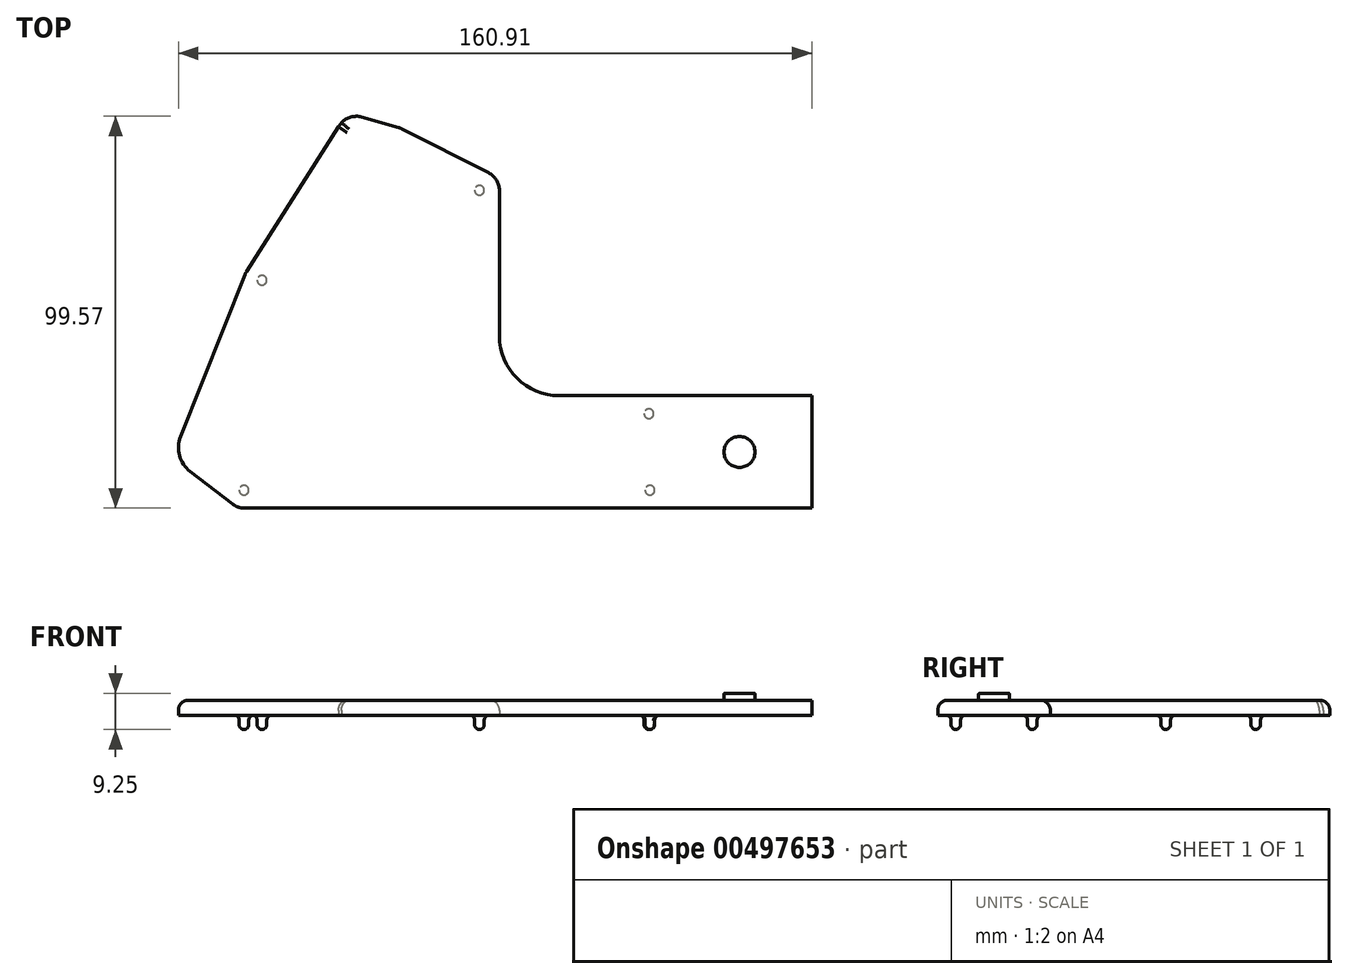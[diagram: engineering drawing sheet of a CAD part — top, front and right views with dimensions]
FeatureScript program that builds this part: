
annotation { "Feature Type Name" : "Feature", "Feature Type Description" : "" }
export const myFeature = defineFeature(function(context is Context, id is Id, definition is map)
    precondition{}
    {
        {
            var Q0;
            Q0=qCreatedBy(makeId("Top.planeOp"),FACE);
            var sketch = newSketch(context, id + "F0", { "sketchPlane" : qUnion([Q0])});
            skLineSegment(sketch, "E0.0", {"start": v(-43.43, -337.67) * mm, "end": v(-15.96, -337.67) * mm});
            skLineSegment(sketch, "E1.0", {"start": v(-160.03, -337.67) * mm, "end": v(-44.7, -337.67) * mm});
            skLineSegment(sketch, "E2.0", {"start": v(-43.43, -309.1) * mm, "end": v(-15.96, -309.1) * mm});
            skLineSegment(sketch, "E3.0", {"start": v(-80.1, -309.1) * mm, "end": v(-44.7, -309.1) * mm});
            skArc(sketch, "E4.0", {"start": v(-80.1, -309.1) * mm, "mid": v(-90.87, -304.63) * mm, "end": v(-95.34, -293.85) * mm});
            skLineSegment(sketch, "E5.0", {"start": v(-95.34, -293.85) * mm, "end": v(-95.34, -256.97) * mm});
            skArc(sketch, "E6.0", {"start": v(-95.34, -256.97) * mm, "mid": v(-96.09, -254.3) * mm, "end": v(-98.12, -252.43) * mm});
            skLineSegment(sketch, "E7.0", {"start": v(-98.12, -252.43) * mm, "end": v(-120.03, -241.33) * mm});
            skArc(sketch, "E8.0", {"start": v(-120.03, -241.33) * mm, "mid": v(-120.47, -241.13) * mm, "end": v(-120.93, -240.97) * mm});
            skLineSegment(sketch, "E9.0", {"start": v(-130.32, -238.3) * mm, "end": v(-120.93, -240.97) * mm});
            skArc(sketch, "E10.0", {"start": v(-130.32, -238.3) * mm, "mid": v(-133.1, -238.29) * mm, "end": v(-135.45, -239.74) * mm});
            skLineSegment(sketch, "E11.0", {"start": v(-136.2, -240.77) * mm, "end": v(-141.2, -248.63) * mm});
            skLineSegment(sketch, "E12.0", {"start": v(-151.3, -264.49) * mm, "end": v(-159.82, -277.9) * mm});
            skLineSegment(sketch, "E13.0", {"start": v(-159.82, -277.9) * mm, "end": v(-165.67, -292.62) * mm});
            skLineSegment(sketch, "E14.0", {"start": v(-172.6, -310.09) * mm, "end": v(-176.33, -319.47) * mm});
            skArc(sketch, "E15.0", {"start": v(-176.33, -319.47) * mm, "mid": v(-176.6, -324.3) * mm, "end": v(-173.9, -328.33) * mm});
            skPoint(sketch, "E16.0", {"position": v(-168.51, -332.47) * mm});
            skLineSegment(sketch, "E17.0", {"start": v(-173.9, -328.33) * mm, "end": v(-163.13, -336.61) * mm});
            skArc(sketch, "E18.0", {"start": v(-163.13, -336.61) * mm, "mid": v(-161.67, -337.4) * mm, "end": v(-160.03, -337.67) * mm});
            skLineSegment(sketch, "E19", {"start": v(-172.6, -310.09) * mm, "end": v(-165.67, -292.62) * mm});
            skLineSegment(sketch, "E20", {"start": v(-151.3, -264.49) * mm, "end": v(-141.2, -248.63) * mm});
            skLineSegment(sketch, "E21", {"start": v(-136.2, -240.77) * mm, "end": v(-135.45, -239.74) * mm});
            skLineSegment(sketch, "E22", {"start": v(-44.7, -309.1) * mm, "end": v(-43.43, -309.1) * mm});
            skLineSegment(sketch, "E23", {"start": v(-44.7, -337.67) * mm, "end": v(-43.43, -337.67) * mm});
            skLineSegment(sketch, "E24", {"start": v(-15.96, -337.67) * mm, "end": v(-15.96, -309.1) * mm});
            skSolve(sketch);
        }
        {
            var Q0;
            Q0=makeQuery(id+"F0.imprint","IMPRINT",FACE,{"disambiguationData":[TD([[makeQuery(id+"F0.imprint","IMPRINT",EDGE,{"derivedFrom":sQuery(id+"F0.wireOp",EDGE,"d1444f51-8acc-4532-b601-094db481933f.0")}),-1.0]])]});
            var Q1;
            Q1=makeQuery(id+"F0.imprint","IMPRINT",FACE,{"disambiguationData":[TD([[makeQuery(id+"F0.imprint","IMPRINT",EDGE,{"derivedFrom":sQuery(id+"F0.wireOp",EDGE,"E0.0")}),1.0]])]});
            var Q2;
            Q2 = qConstructionFilter(qBodyType(qCreatedBy(id + "F0" ,EDGE), BodyType.WIRE), ConstructionObject.NO);
            extrude(context, id + "F1", {"entities" : qUnion([Q0, Q1]), "surfaceEntities" : qUnion([Q2]), "depth" : 3.81 * mm, "offsetDistance" : 25.4 * mm});
        }
        {
            var Q0;
            Q0=makeQuery(id+"F1.opExtrude","CAP_EDGE",EDGE,{"disambiguationData":[OSD([sQuery(id+"F0.wireOp",EDGE,"E21")])],"isStart":false});
            var Q1;
            Q1=makeQuery(id+"F1.opExtrude","CAP_EDGE",EDGE,{"disambiguationData":[OSD([sQuery(id+"F0.wireOp",EDGE,"E9.0")])],"isStart":false});
            var Q2;
            Q2=makeQuery(id+"F1.opExtrude","CAP_EDGE",EDGE,{"disambiguationData":[OSD([sQuery(id+"F0.wireOp",EDGE,"E0.0"),sQuery(id+"F0.wireOp",EDGE,"E1.0"),sQuery(id+"F0.wireOp",EDGE,"E23")])],"isStart":false});
            fillet(context, id + "F2", {"entities" : qUnion([Q0, Q1, Q2]), "radius" : 2.54 * mm, "tangentPropagation" : true, "allowEdgeOverflow" : false});
        }
        {
            var Q0;
            Q0=makeQuery(id+"F1.opExtrude","CAP_FACE",FACE,{"disambiguationData":[OSD([sQuery(id+"F0.wireOp",EDGE,"E0.0"),sQuery(id+"F0.wireOp",EDGE,"E1.0"),sQuery(id+"F0.wireOp",EDGE,"E2.0"),sQuery(id+"F0.wireOp",EDGE,"E3.0"),sQuery(id+"F0.wireOp",EDGE,"E4.0"),sQuery(id+"F0.wireOp",EDGE,"E5.0"),sQuery(id+"F0.wireOp",EDGE,"E6.0"),sQuery(id+"F0.wireOp",EDGE,"E7.0"),sQuery(id+"F0.wireOp",EDGE,"E8.0"),sQuery(id+"F0.wireOp",EDGE,"E9.0"),sQuery(id+"F0.wireOp",EDGE,"E10.0"),sQuery(id+"F0.wireOp",EDGE,"E11.0"),sQuery(id+"F0.wireOp",EDGE,"E12.0"),sQuery(id+"F0.wireOp",EDGE,"E13.0"),sQuery(id+"F0.wireOp",EDGE,"E14.0"),sQuery(id+"F0.wireOp",EDGE,"E15.0"),sQuery(id+"F0.wireOp",EDGE,"E17.0"),sQuery(id+"F0.wireOp",EDGE,"E18.0"),sQuery(id+"F0.wireOp",EDGE,"E19"),sQuery(id+"F0.wireOp",EDGE,"E20"),sQuery(id+"F0.wireOp",EDGE,"E21"),sQuery(id+"F0.wireOp",EDGE,"E22"),sQuery(id+"F0.wireOp",EDGE,"E23"),sQuery(id+"F0.wireOp",EDGE,"E24")])],"isStart":false});
            var sketch = newSketch(context, id + "F3", { "sketchPlane" : qUnion([Q0])});
            skCircle(sketch, "E25.0", {"center": v(-34.35, -323.38) * mm, "radius": 3.94 * mm});
            skLineSegment(sketch, "E26", {"start": v(-97.88, -323.38) * mm, "end": v(-34.35, -323.38) * mm});
            skLineSegment(sketch, "E27", {"start": v(-97.88, -293.85) * mm, "end": v(-97.88, -335.13) * mm});
            skLineSegment(sketch, "E28", {"start": v(-34.35, -323.38) * mm, "end": v(-34.35, -311.63) * mm});
            skLineSegment(sketch, "E29", {"start": v(-34.35, -323.38) * mm, "end": v(-34.35, -335.13) * mm});
            skSolve(sketch);
        }
        {
            var Q0;
            Q0 = qSketchRegion(id + "F3", true);
            extrude(context, id + "F4", {"entities" : qUnion([Q0]), "operationType" : NewBodyOperationType.ADD, "depth" : 1.78 * mm});
        }
        {
            var Q0;
            Q0=makeQuery(id+"F1.opExtrude","SWEPT_EDGE",EDGE,{"disambiguationData":[OSD([sQuery(id+"F0.wireOp",EDGE,"E12.0"),sQuery(id+"F0.wireOp",EDGE,"E13.0")])]});
            fillet(context, id + "F5", {"entities" : qUnion([Q0]), "radius" : 5.08 * mm, "tangentPropagation" : true, "allowEdgeOverflow" : false});
        }
        {
            var Q0;
            Q0=makeQuery(id+"F1.opExtrude","CAP_FACE",FACE,{"disambiguationData":[OSD([sQuery(id+"F0.wireOp",EDGE,"E0.0"),sQuery(id+"F0.wireOp",EDGE,"E1.0"),sQuery(id+"F0.wireOp",EDGE,"E2.0"),sQuery(id+"F0.wireOp",EDGE,"E3.0"),sQuery(id+"F0.wireOp",EDGE,"E4.0"),sQuery(id+"F0.wireOp",EDGE,"E5.0"),sQuery(id+"F0.wireOp",EDGE,"E6.0"),sQuery(id+"F0.wireOp",EDGE,"E7.0"),sQuery(id+"F0.wireOp",EDGE,"E8.0"),sQuery(id+"F0.wireOp",EDGE,"E9.0"),sQuery(id+"F0.wireOp",EDGE,"E10.0"),sQuery(id+"F0.wireOp",EDGE,"E11.0"),sQuery(id+"F0.wireOp",EDGE,"E12.0"),sQuery(id+"F0.wireOp",EDGE,"E13.0"),sQuery(id+"F0.wireOp",EDGE,"E14.0"),sQuery(id+"F0.wireOp",EDGE,"E15.0"),sQuery(id+"F0.wireOp",EDGE,"E17.0"),sQuery(id+"F0.wireOp",EDGE,"E18.0"),sQuery(id+"F0.wireOp",EDGE,"E19"),sQuery(id+"F0.wireOp",EDGE,"E20"),sQuery(id+"F0.wireOp",EDGE,"E21"),sQuery(id+"F0.wireOp",EDGE,"E22"),sQuery(id+"F0.wireOp",EDGE,"E23"),sQuery(id+"F0.wireOp",EDGE,"E24")])],"isStart":true});
            var sketch = newSketch(context, id + "F6", { "sketchPlane" : qUnion([Q0])});
            skLineSegment(sketch, "E30", {"start": v(-57.11, 333.03) * mm, "end": v(-57.11, 337.67) * mm});
            skLineSegment(sketch, "E31", {"start": v(-125.27, 333.03) * mm, "end": v(-9.65, 333.03) * mm});
            skSolve(sketch);
        }
        {
            var Q0;
            Q0=makeQuery(id+"F1.opExtrude","SWEPT_FACE",FACE,{"disambiguationData":[OSD([sQuery(id+"F0.wireOp",EDGE,"E0.0"),sQuery(id+"F0.wireOp",EDGE,"E1.0"),sQuery(id+"F0.wireOp",EDGE,"E23")])]});
            cPlane(context, id + "F7", {"entities" : qUnion([Q0]), "cplaneType" : CPlaneType.OFFSET, "offset" : 4.57 * mm, "oppositeDirection" : true, "width" : 152.4 * mm, "height" : 152.4 * mm});
        }
        {
            var Q0;
            Q0=qCreatedBy(id+"F7.planeOp",FACE);
            var sketch = newSketch(context, id + "F8", { "sketchPlane" : qUnion([Q0])});
            skLineSegment(sketch, "E32.bottom", {"start": v(-58.33, -2.39) * mm, "end": v(-58.33, -1.27) * mm});
            skLineSegment(sketch, "E32.left", {"start": v(-37.58, -6.33) * mm, "end": v(-37.58, -6.33) * mm});
            skPoint(sketch, "E33.visualSharp", {"position": v(-36.99, -12.97) * mm});
            skPoint(sketch, "E34.visualSharp", {"position": v(-58.33, -12.97) * mm});
            skArc(sketch, "E34.filletArc", {"start": v(-58.33, -2.39) * mm, "mid": v(-57.96, -3.28) * mm, "end": v(-57.06, -3.66) * mm});
            skLineSegment(sketch, "E35", {"start": v(-59.6, 0) * mm, "end": v(-60.04, 0) * mm});
            skArc(sketch, "E36.filletArc", {"start": v(-58.33, -1.27) * mm, "mid": v(-58.7, -0.37) * mm, "end": v(-59.6, 0) * mm});
            skLineSegment(sketch, "E37", {"start": v(-60.04, 0) * mm, "end": v(-54.18, 0) * mm});
            skLineSegment(sketch, "E38", {"start": v(-58.33, -1.27) * mm, "end": v(-58.33, 0) * mm});
            skLineSegment(sketch, "E39", {"start": v(-57.11, -3.66) * mm, "end": v(-57.11, 0) * mm});
            skSolve(sketch);
        }
        {
            var Q0;
            {var subQ5=sQuery(id+"F8.wireOp",EDGE,"E32.bottom");Q0=makeQuery(id+"F8.imprint","IMPRINT",FACE,{"disambiguationData":[TD([[makeQuery(id+"F8.imprint","IMPRINT",EDGE,{"derivedFrom":subQ5}),-1.0]])]});}
            var Q1;
            {var subQ0=sQuery(id+"F8.wireOp",EDGE,"E36.filletArc");Q1=makeQuery(id+"F8.imprint","IMPRINT",FACE,{"disambiguationData":[TD([[makeQuery(id+"F8.imprint","IMPRINT",EDGE,{"derivedFrom":subQ0}),-1.0]])]});}
            var Q2;
            Q2=sQuery(id+"F8.wireOp",EDGE,"E32.bottom");
            var Q3;
            Q3=sQuery(id+"F8.wireOp",EDGE,"E34.filletArc");
            var Q4;
            Q4=sQuery(id+"F8.wireOp",EDGE,"E39");
            var Q5;
            Q5=sQuery(id+"F8.wireOp",EDGE,"E38");
            var Q6;
            Q6=sQuery(id+"F8.wireOp",EDGE,"E36.filletArc");
            var Q7;
            Q7=sQuery(id+"F8.wireOp",EDGE,"E35");
            var Q8;
            Q8=sQuery(id+"F8.wireOp",EDGE,"E37");
            var Q9;
            Q9=sQuery(id+"F8.wireOp",EDGE,"E39");
            revolve(context, id + "F9", {"operationType" : NewBodyOperationType.ADD, "entities" : qUnion([Q0, Q1]), "surfaceEntities" : qUnion([Q2, Q3, Q4, Q5, Q6, Q7, Q8]), "axis" : qUnion([Q9]), "revolveType" : RevolveType.FULL});
        }
        {
            var Q0;
            {var subQ6=sQuery(id+"F6.wireOp",EDGE,"E30");Q0=makeQuery(id+"F6.imprint","IMPRINT",FACE,{"disambiguationData":[TD([[makeQuery(id+"F6.imprint","IMPRINT",EDGE,{"derivedFrom":subQ6}),1.0]])]});}
            var sketch = newSketch(context, id + "F10", { "sketchPlane" : qUnion([Q0])});
            skLineSegment(sketch, "E40", {"start": v(-15.96, 313.66) * mm, "end": v(-57.36, 313.66) * mm});
            skLineSegment(sketch, "E41", {"start": v(-57.36, 309.1) * mm, "end": v(-57.36, 313.66) * mm});
            skLineSegment(sketch, "E42.0", {"start": v(-80.1, 309.1) * mm, "end": v(-15.96, 309.1) * mm});
            skLineSegment(sketch, "E43.0", {"start": v(-15.96, 337.67) * mm, "end": v(-15.96, 309.1) * mm});
            skSolve(sketch);
        }
        {
            var Q0;
            Q0=makeQuery(id+"F1.opExtrude","SWEPT_FACE",FACE,{"disambiguationData":[OSD([sQuery(id+"F0.wireOp",EDGE,"E2.0"),sQuery(id+"F0.wireOp",EDGE,"E3.0"),sQuery(id+"F0.wireOp",EDGE,"E22")])]});
            cPlane(context, id + "F11", {"entities" : qUnion([Q0]), "cplaneType" : CPlaneType.OFFSET, "offset" : 4.57 * mm, "oppositeDirection" : true, "width" : 152.4 * mm, "height" : 152.4 * mm});
        }
        {
            var Q0;
            Q0=qCreatedBy(id+"F11.planeOp",FACE);
            var sketch = newSketch(context, id + "F12", { "sketchPlane" : qUnion([Q0])});
            skLineSegment(sketch, "E44.bottom", {"start": v(56.15, -2.39) * mm, "end": v(56.15, -1.27) * mm});
            skArc(sketch, "E45.filletArc", {"start": v(56.15, -2.39) * mm, "mid": v(56.52, -3.28) * mm, "end": v(57.42, -3.66) * mm});
            skLineSegment(sketch, "E46", {"start": v(54.88, 0) * mm, "end": v(54.43, 0) * mm});
            skArc(sketch, "E47.filletArc", {"start": v(56.15, -1.27) * mm, "mid": v(55.77, -0.37) * mm, "end": v(54.88, 0) * mm});
            skLineSegment(sketch, "E48", {"start": v(54.43, 0) * mm, "end": v(60.3, 0) * mm});
            skLineSegment(sketch, "E49", {"start": v(56.15, -1.27) * mm, "end": v(56.15, 0) * mm});
            skLineSegment(sketch, "E50", {"start": v(57.36, -3.66) * mm, "end": v(57.36, 0) * mm});
            skSolve(sketch);
        }
        {
            var Q0;
            Q0 = qSketchRegion(id + "F12", true);
            var Q1;
            Q1=sQuery(id+"F12.wireOp",EDGE,"E50");
            revolve(context, id + "F13", {"operationType" : NewBodyOperationType.ADD, "entities" : qUnion([Q0]), "axis" : qUnion([Q1]), "revolveType" : RevolveType.FULL});
        }
        {
            var Q0;
            {var subQ6=sQuery(id+"F6.wireOp",EDGE,"E30");Q0=makeQuery(id+"F6.imprint","IMPRINT",FACE,{"disambiguationData":[TD([[makeQuery(id+"F6.imprint","IMPRINT",EDGE,{"derivedFrom":subQ6}),1.0]])]});}
            var sketch = newSketch(context, id + "F14", { "sketchPlane" : qUnion([Q0])});
            skLineSegment(sketch, "E51", {"start": v(-100.42, 256.9) * mm, "end": v(-100.42, 363.43) * mm});
            skLineSegment(sketch, "E52", {"start": v(-95.34, 256.9) * mm, "end": v(-100.42, 256.9) * mm});
            skLineSegment(sketch, "E53.0", {"start": v(-95.34, 293.85) * mm, "end": v(-95.34, 256.97) * mm});
            skArc(sketch, "E54.0", {"start": v(-95.34, 256.97) * mm, "mid": v(-96.09, 254.3) * mm, "end": v(-98.12, 252.43) * mm});
            skSolve(sketch);
        }
        {
            var Q0;
            Q0=makeQuery(id+"F1.opExtrude","SWEPT_FACE",FACE,{"disambiguationData":[OSD([sQuery(id+"F0.wireOp",EDGE,"E0.0"),sQuery(id+"F0.wireOp",EDGE,"E1.0"),sQuery(id+"F0.wireOp",EDGE,"E23")])]});
            cPlane(context, id + "F15", {"entities" : qUnion([Q0]), "cplaneType" : CPlaneType.OFFSET, "offset" : 80.77 * mm, "oppositeDirection" : true, "width" : 152.4 * mm, "height" : 152.4 * mm});
        }
        {
            var Q0;
            Q0=qCreatedBy(id+"F15.planeOp",FACE);
            var sketch = newSketch(context, id + "F16", { "sketchPlane" : qUnion([Q0])});
            skLineSegment(sketch, "E55.bottom", {"start": v(-101.64, -2.39) * mm, "end": v(-101.64, -1.27) * mm});
            skArc(sketch, "E56.filletArc", {"start": v(-101.64, -2.39) * mm, "mid": v(-101.27, -3.28) * mm, "end": v(-100.37, -3.66) * mm});
            skLineSegment(sketch, "E57", {"start": v(-102.9, 0) * mm, "end": v(-103.35, 0) * mm});
            skArc(sketch, "E58.filletArc", {"start": v(-101.64, -1.27) * mm, "mid": v(-102, -0.37) * mm, "end": v(-102.9, 0) * mm});
            skLineSegment(sketch, "E59", {"start": v(-103.35, 0) * mm, "end": v(-97.48, 0) * mm});
            skLineSegment(sketch, "E60", {"start": v(-101.64, -1.27) * mm, "end": v(-101.64, 0) * mm});
            skLineSegment(sketch, "E61", {"start": v(-100.42, -3.66) * mm, "end": v(-100.42, 0) * mm});
            skSolve(sketch);
        }
        {
            var Q0;
            Q0 = qSketchRegion(id + "F16", true);
            var Q1;
            Q1=sQuery(id+"F16.wireOp",EDGE,"E61");
            revolve(context, id + "F17", {"operationType" : NewBodyOperationType.ADD, "entities" : qUnion([Q0]), "axis" : qUnion([Q1]), "revolveType" : RevolveType.FULL});
        }
        {
            var Q0;
            {var subQ6=sQuery(id+"F6.wireOp",EDGE,"E30");Q0=makeQuery(id+"F6.imprint","IMPRINT",FACE,{"disambiguationData":[TD([[makeQuery(id+"F6.imprint","IMPRINT",EDGE,{"derivedFrom":subQ6}),1.0]])]});}
            var sketch = newSketch(context, id + "F18", { "sketchPlane" : qUnion([Q0])});
            skLineSegment(sketch, "E62", {"start": v(-160.23, 333.1) * mm, "end": v(-160.23, 337.66) * mm});
            skLineSegment(sketch, "E63", {"start": v(-100.12, 333.1) * mm, "end": v(-163.57, 333.1) * mm});
            skSolve(sketch);
        }
        {
            var Q0;
            Q0=qCreatedBy(id+"F7.planeOp",FACE);
            var sketch = newSketch(context, id + "F19", { "sketchPlane" : qUnion([Q0])});
            skLineSegment(sketch, "E64.bottom", {"start": v(-161.45, -2.39) * mm, "end": v(-161.45, -1.27) * mm});
            skArc(sketch, "E65.filletArc", {"start": v(-161.45, -2.39) * mm, "mid": v(-161.08, -3.28) * mm, "end": v(-160.18, -3.66) * mm});
            skLineSegment(sketch, "E66", {"start": v(-162.72, 0) * mm, "end": v(-163.17, 0) * mm});
            skArc(sketch, "E67.filletArc", {"start": v(-161.45, -1.27) * mm, "mid": v(-161.83, -0.37) * mm, "end": v(-162.72, 0) * mm});
            skLineSegment(sketch, "E68", {"start": v(-163.17, 0) * mm, "end": v(-157.3, 0) * mm});
            skLineSegment(sketch, "E69", {"start": v(-161.45, -1.27) * mm, "end": v(-161.45, 0) * mm});
            skLineSegment(sketch, "E70", {"start": v(-160.23, -3.66) * mm, "end": v(-160.23, 0) * mm});
            skSolve(sketch);
        }
        {
            var Q0;
            Q0 = qSketchRegion(id + "F19", true);
            var Q1;
            Q1=sQuery(id+"F19.wireOp",EDGE,"E70");
            revolve(context, id + "F20", {"operationType" : NewBodyOperationType.ADD, "entities" : qUnion([Q0]), "axis" : qUnion([Q1]), "revolveType" : RevolveType.FULL});
        }
        {
            var Q0;
            {var subQ6=sQuery(id+"F6.wireOp",EDGE,"E30");Q0=makeQuery(id+"F6.imprint","IMPRINT",FACE,{"disambiguationData":[TD([[makeQuery(id+"F6.imprint","IMPRINT",EDGE,{"derivedFrom":subQ6}),1.0]])]});}
            var sketch = newSketch(context, id + "F21", { "sketchPlane" : qUnion([Q0])});
            skLineSegment(sketch, "E71", {"start": v(-155.66, 279.75) * mm, "end": v(-155.66, 448.27) * mm});
            skLineSegment(sketch, "E72", {"start": v(-46.55, 279.75) * mm, "end": v(-228.58, 279.75) * mm});
            skLineSegment(sketch, "E73.0", {"start": v(-136.2, 240.77) * mm, "end": v(-159.56, 277.49) * mm});
            skLineSegment(sketch, "E74.0", {"start": v(-176.33, 319.47) * mm, "end": v(-160, 278.34) * mm});
            skArc(sketch, "E75.0", {"start": v(-160, 278.34) * mm, "mid": v(-159.8, 277.9) * mm, "end": v(-159.56, 277.49) * mm});
            skSolve(sketch);
        }
        {
            var Q0;
            Q0=makeQuery(id+"F1.opExtrude","SWEPT_FACE",FACE,{"disambiguationData":[OSD([sQuery(id+"F0.wireOp",EDGE,"E0.0"),sQuery(id+"F0.wireOp",EDGE,"E1.0"),sQuery(id+"F0.wireOp",EDGE,"E23")])]});
            cPlane(context, id + "F22", {"entities" : qUnion([Q0]), "cplaneType" : CPlaneType.OFFSET, "offset" : 57.9 * mm, "oppositeDirection" : true, "width" : 152.4 * mm, "height" : 152.4 * mm});
        }
        {
            var Q0;
            Q0=qCreatedBy(id+"F22.planeOp",FACE);
            var sketch = newSketch(context, id + "F23", { "sketchPlane" : qUnion([Q0])});
            skLineSegment(sketch, "E76.bottom", {"start": v(-156.88, -2.39) * mm, "end": v(-156.88, -1.27) * mm});
            skArc(sketch, "E77.filletArc", {"start": v(-156.88, -2.39) * mm, "mid": v(-156.51, -3.28) * mm, "end": v(-155.61, -3.66) * mm});
            skLineSegment(sketch, "E78", {"start": v(-158.15, 0) * mm, "end": v(-158.6, 0) * mm});
            skArc(sketch, "E79.filletArc", {"start": v(-156.88, -1.27) * mm, "mid": v(-157.25, -0.37) * mm, "end": v(-158.15, 0) * mm});
            skLineSegment(sketch, "E80", {"start": v(-158.6, 0) * mm, "end": v(-152.73, 0) * mm});
            skLineSegment(sketch, "E81", {"start": v(-156.88, -1.27) * mm, "end": v(-156.88, 0) * mm});
            skLineSegment(sketch, "E82", {"start": v(-155.66, -3.66) * mm, "end": v(-155.66, 0) * mm});
            skSolve(sketch);
        }
        {
            var Q0;
            Q0 = qSketchRegion(id + "F23", true);
            var Q1;
            Q1=sQuery(id+"F23.wireOp",EDGE,"E82");
            revolve(context, id + "F24", {"operationType" : NewBodyOperationType.ADD, "entities" : qUnion([Q0]), "axis" : qUnion([Q1]), "revolveType" : RevolveType.FULL});
        }
        {
            var Q0;
            Q0=makeQuery(id+"F4.opExtrude","CAP_EDGE",EDGE,{"disambiguationData":[OSD([sQuery(id+"F3.wireOp",EDGE,"E25.0")])],"isStart":false});
            fillet(context, id + "F25", {"entities" : qUnion([Q0]), "radius" : 0.25 * mm, "tangentPropagation" : true, "allowEdgeOverflow" : false});
        }
    });
